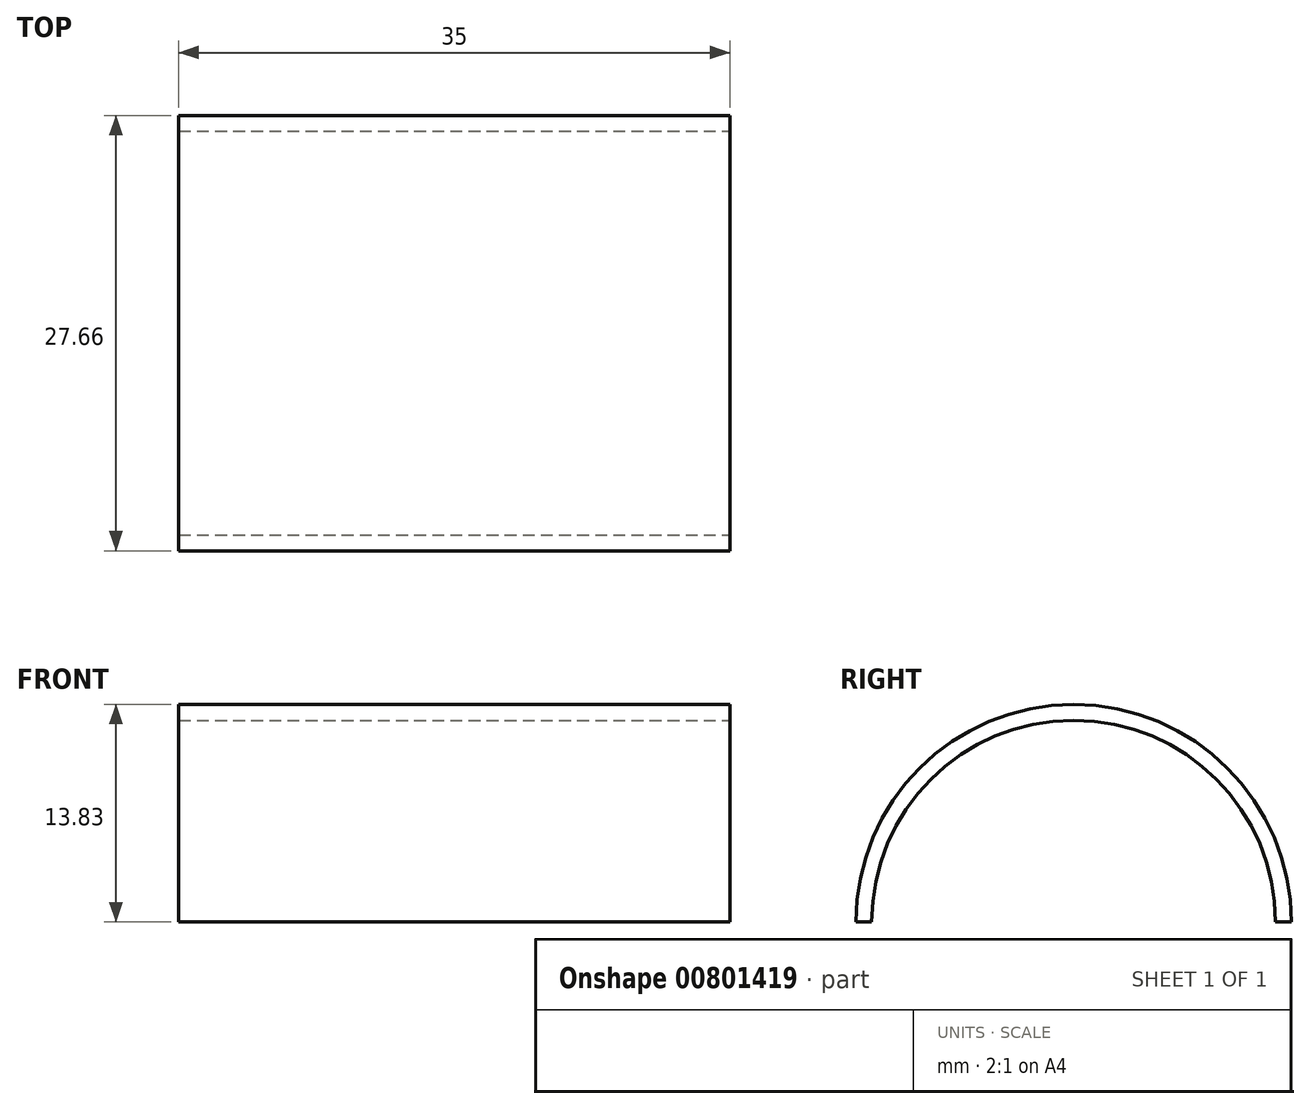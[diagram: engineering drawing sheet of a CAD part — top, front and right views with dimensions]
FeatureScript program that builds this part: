
annotation { "Feature Type Name" : "Feature", "Feature Type Description" : "" }
export const myFeature = defineFeature(function(context is Context, id is Id, definition is map)
    precondition{}
    {
        {
            var Q0;
            Q0=qCreatedBy(makeId("Right.planeOp"),FACE);
            var sketch = newSketch(context, id + "F0", { "sketchPlane" : qUnion([Q0])});
            skCircle(sketch, "E0", {"center": v(0, 0) * mm, "radius": 12.82 * mm});
            skCircle(sketch, "E1.0", {"center": v(0, 0) * mm, "radius": 13.83 * mm});
            skSolve(sketch);
        }
        {
            var Q0;
            Q0 = qSketchRegion(id + "F0", true);
            extrude(context, id + "F1", {"entities" : qUnion([Q0]), "endBound" : BoundingType.SYMMETRIC, "oppositeDirection" : true, "depth" : 35 * mm, "offsetDistance" : 25 * mm});
        }
        {
            var Q0;
            Q0=qCreatedBy(makeId("Right.planeOp"),FACE);
            var sketch = newSketch(context, id + "F2", { "sketchPlane" : qUnion([Q0])});
            skLineSegment(sketch, "E2.bottom", {"start": v(25, 0) * mm, "end": v(-25, 0) * mm});
            skLineSegment(sketch, "E2.top", {"start": v(25, -20) * mm, "end": v(-25, -20) * mm});
            skLineSegment(sketch, "E2.left", {"start": v(25, 0) * mm, "end": v(25, -20) * mm});
            skLineSegment(sketch, "E2.right", {"start": v(-25, 0) * mm, "end": v(-25, -20) * mm});
            skSolve(sketch);
        }
        {
            var Q0;
            Q0 = qSketchRegion(id + "F2", true);
            extrude(context, id + "F3", {"entities" : qUnion([Q0]), "operationType" : NewBodyOperationType.REMOVE, "endBound" : BoundingType.SYMMETRIC, "oppositeDirection" : true, "depth" : 50 * mm, "offsetDistance" : 25 * mm});
        }
    });
